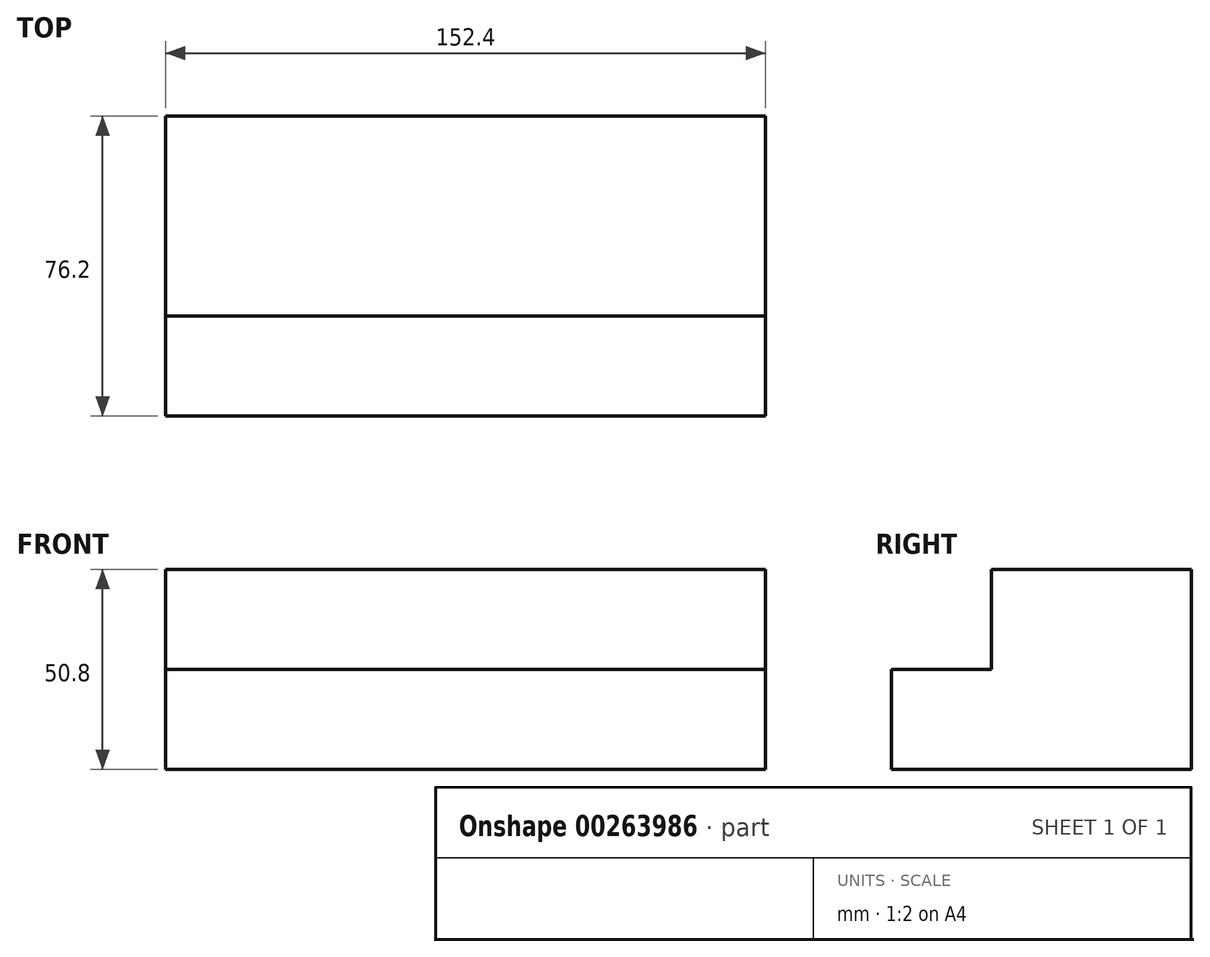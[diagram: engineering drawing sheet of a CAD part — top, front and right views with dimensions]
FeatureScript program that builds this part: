
annotation { "Feature Type Name" : "Feature", "Feature Type Description" : "" }
export const myFeature = defineFeature(function(context is Context, id is Id, definition is map)
    precondition{}
    {
        {
            var Q0;
            Q0=qCreatedBy(makeId("Right.planeOp"),FACE);
            var sketch = newSketch(context, id + "F0", { "sketchPlane" : qUnion([Q0])});
            skLineSegment(sketch, "E0", {"start": v(0, 0) * mm, "end": v(76.2, 0) * mm});
            skLineSegment(sketch, "E1", {"start": v(76.2, 0) * mm, "end": v(76.2, 50.8) * mm});
            skLineSegment(sketch, "E2", {"start": v(76.2, 50.8) * mm, "end": v(25.4, 50.8) * mm});
            skLineSegment(sketch, "E3", {"start": v(25.4, 50.8) * mm, "end": v(25.4, 25.4) * mm});
            skLineSegment(sketch, "E4", {"start": v(25.4, 25.4) * mm, "end": v(0, 25.4) * mm});
            skLineSegment(sketch, "E5", {"start": v(0, 25.4) * mm, "end": v(0, 0) * mm});
            skSolve(sketch);
        }
        {
            var Q0;
            Q0 = qSketchRegion(id + "F0", true);
            extrude(context, id + "F1", {"entities" : qUnion([Q0]), "oppositeDirection" : true, "depth" : 152.4 * mm});
        }
    });
